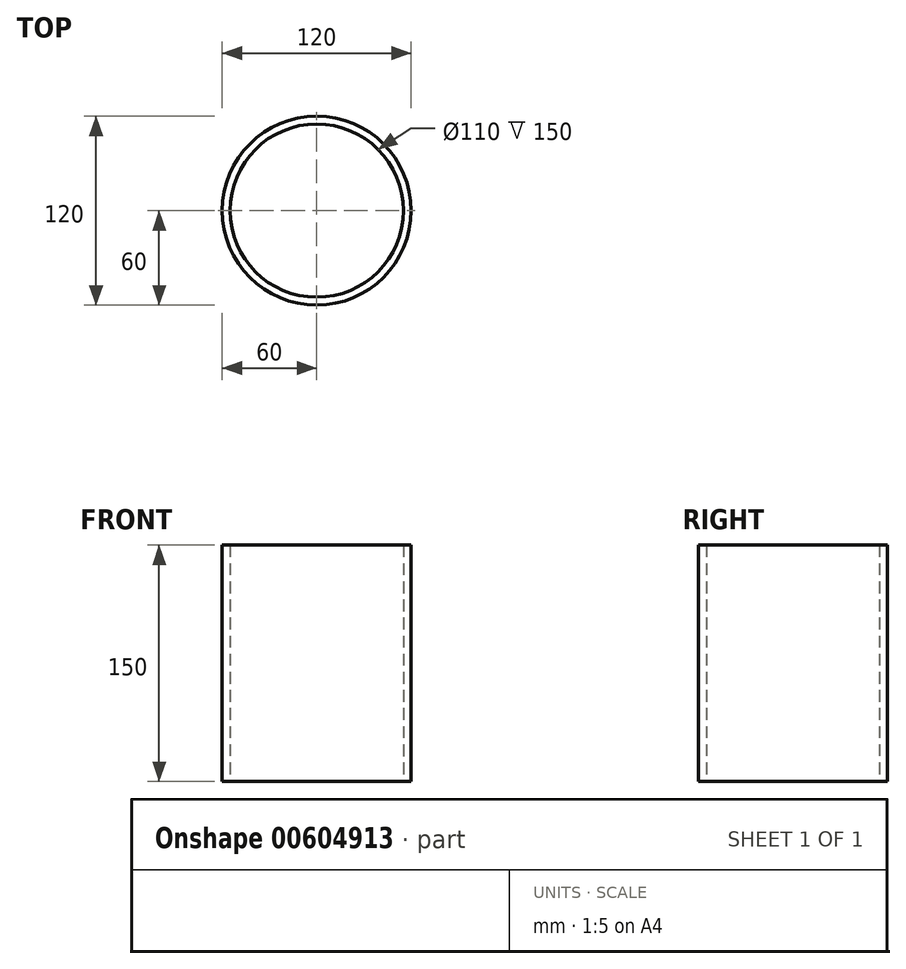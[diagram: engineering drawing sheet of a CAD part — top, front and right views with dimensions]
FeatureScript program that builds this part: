
annotation { "Feature Type Name" : "Feature", "Feature Type Description" : "" }
export const myFeature = defineFeature(function(context is Context, id is Id, definition is map)
    precondition{}
    {
        {
            var Q0;
            Q0=qCreatedBy(makeId("Top.planeOp"),FACE);
            var sketch = newSketch(context, id + "F0", { "sketchPlane" : qUnion([Q0])});
            skCircle(sketch, "E0", {"center": v(0, 0) * mm, "radius": 55 * mm});
            skCircle(sketch, "E1", {"center": v(0, 0) * mm, "radius": 60 * mm});
            skSolve(sketch);
        }
        {
            var Q0;
            Q0 = qSketchRegion(id + "F0", true);
            extrude(context, id + "F1", {"entities" : qUnion([Q0]), "depth" : 150 * mm, "offsetDistance" : 25 * mm});
        }
    });
